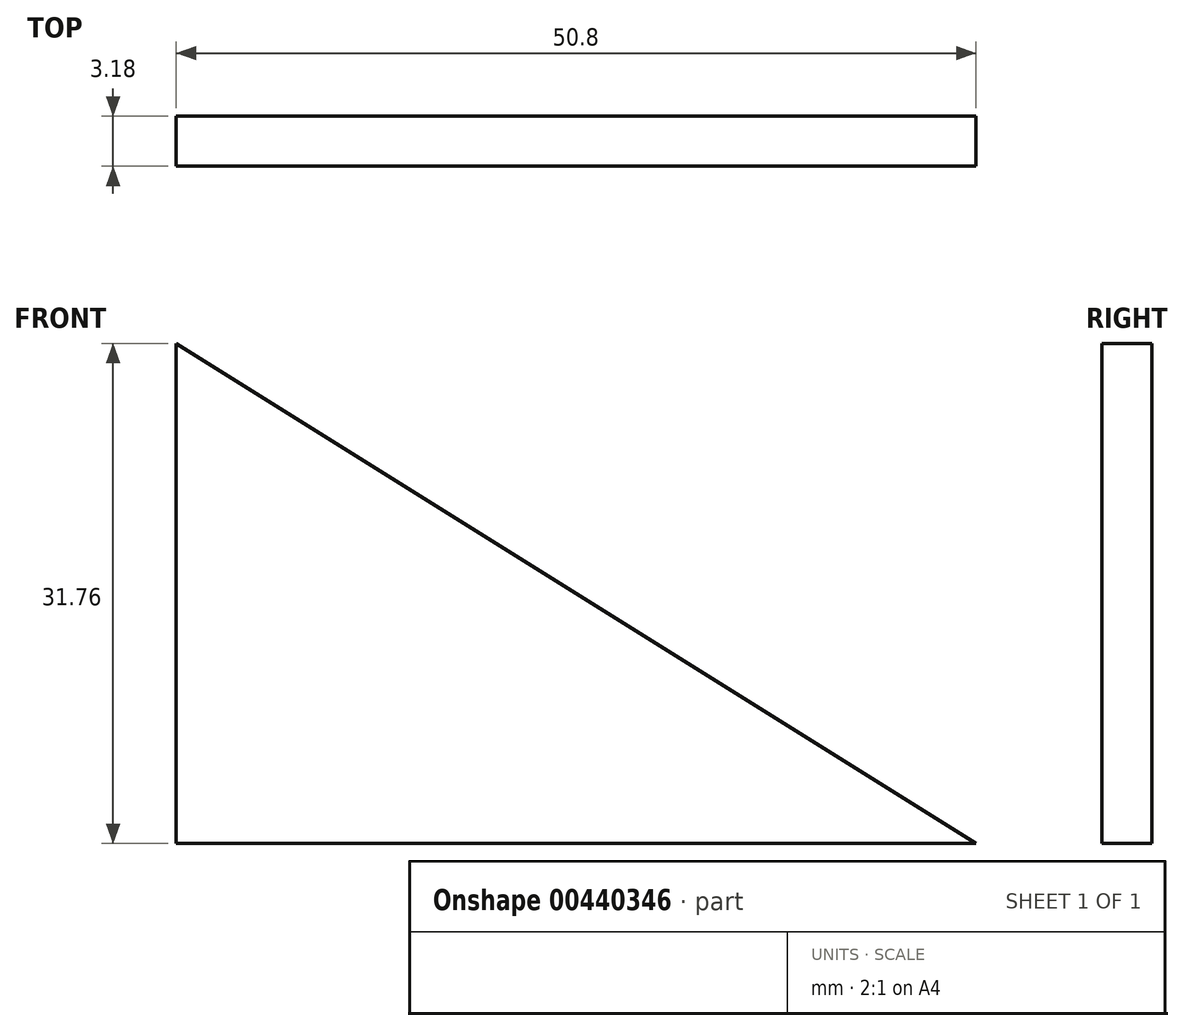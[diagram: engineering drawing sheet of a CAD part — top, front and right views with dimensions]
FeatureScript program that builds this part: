
annotation { "Feature Type Name" : "Feature", "Feature Type Description" : "" }
export const myFeature = defineFeature(function(context is Context, id is Id, definition is map)
    precondition{}
    {
        {
            var Q0;
            Q0=qCreatedBy(makeId("Front.planeOp"),FACE);
            var sketch = newSketch(context, id + "F0", { "sketchPlane" : qUnion([Q0])});
            skLineSegment(sketch, "E0.bottom", {"start": v(-25.4, 15.87) * mm, "end": v(25.4, 15.87) * mm});
            skLineSegment(sketch, "E0.top", {"start": v(-25.4, -15.87) * mm, "end": v(25.4, -15.87) * mm});
            skLineSegment(sketch, "E0.left", {"start": v(-25.4, 15.88) * mm, "end": v(-25.4, -15.87) * mm});
            skLineSegment(sketch, "E0.right", {"start": v(25.4, 15.87) * mm, "end": v(25.4, -15.87) * mm});
            skPoint(sketch, "E0.middle", {"position": v(0, 0) * mm});
            skLineSegment(sketch, "E1", {"start": v(-25.4, 15.87) * mm, "end": v(25.4, -15.87) * mm});
            skSolve(sketch);
        }
        {
            var Q0;
            Q0=makeQuery(id+"F0.imprint","IMPRINT",FACE,{"disambiguationData":[TD([[makeQuery(id+"F0.imprint","IMPRINT",EDGE,{"derivedFrom":sQuery(id+"F0.wireOp",EDGE,"E0.top")}),1.0]])]});
            extrude(context, id + "F1", {"entities" : qUnion([Q0]), "endBound" : BoundingType.SYMMETRIC, "depth" : 3.17 * mm});
        }
    });
